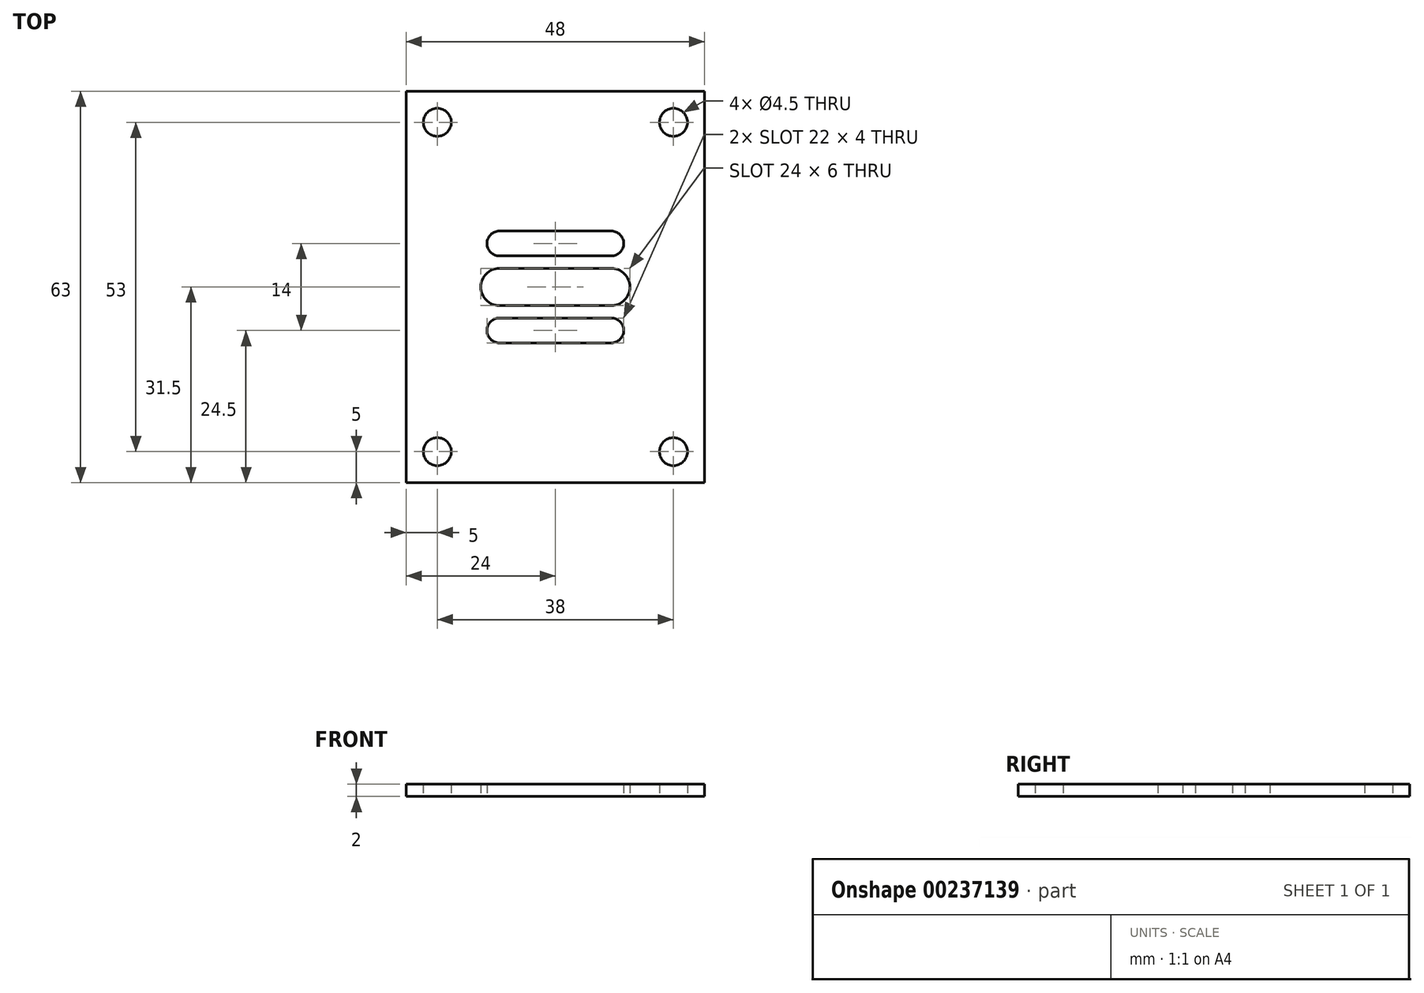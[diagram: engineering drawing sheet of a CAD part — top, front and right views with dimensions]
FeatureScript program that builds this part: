
annotation { "Feature Type Name" : "Feature", "Feature Type Description" : "" }
export const myFeature = defineFeature(function(context is Context, id is Id, definition is map)
    precondition{}
    {
        {
            var Q0;
            Q0=qCreatedBy(makeId("Top.planeOp"),FACE);
            var sketch = newSketch(context, id + "F0", { "sketchPlane" : qUnion([Q0])});
            skLineSegment(sketch, "E0.top", {"start": v(-24, -31.5) * mm, "end": v(24, -31.5) * mm});
            skLineSegment(sketch, "E0.left", {"start": v(-24, 31.5) * mm, "end": v(-24, -31.5) * mm});
            skLineSegment(sketch, "E0.right", {"start": v(24, 31.5) * mm, "end": v(24, -31.5) * mm});
            skPoint(sketch, "E0.middle", {"position": v(0, 0) * mm});
            skLineSegment(sketch, "E1.bottom", {"start": v(-9, 3) * mm, "end": v(9, 3) * mm});
            skLineSegment(sketch, "E1.top", {"start": v(-9, -3) * mm, "end": v(9, -3) * mm});
            skLineSegment(sketch, "E1.left", {"start": v(-12, 0) * mm, "end": v(-12, 0) * mm});
            skLineSegment(sketch, "E1.right", {"start": v(12, 0) * mm, "end": v(12, 0) * mm});
            skArc(sketch, "E2.filletArc", {"start": v(-9, 3) * mm, "mid": v(-11.12, 2.12) * mm, "end": v(-12, 0) * mm});
            skArc(sketch, "E3.filletArc", {"start": v(9, -3) * mm, "mid": v(11.12, -2.12) * mm, "end": v(12, 0) * mm});
            skArc(sketch, "E4.filletArc", {"start": v(12, 0) * mm, "mid": v(11.12, 2.12) * mm, "end": v(9, 3) * mm});
            skArc(sketch, "E5.filletArc", {"start": v(-12, 0) * mm, "mid": v(-11.12, -2.12) * mm, "end": v(-9, -3) * mm});
            skLineSegment(sketch, "E6", {"start": v(-9, 0) * mm, "end": v(-6.45, 0) * mm});
            skLineSegment(sketch, "E7", {"start": v(9, 0) * mm, "end": v(6, 0) * mm});
            skLineSegment(sketch, "E8", {"start": v(4, 0) * mm, "end": v(-4, 0) * mm});
            skLineSegment(sketch, "E9.bottom", {"start": v(-9, -9) * mm, "end": v(9, -9) * mm});
            skLineSegment(sketch, "E9.top", {"start": v(-9, -5) * mm, "end": v(9, -5) * mm});
            skLineSegment(sketch, "E9.left", {"start": v(-11, -7) * mm, "end": v(-11, -7) * mm});
            skLineSegment(sketch, "E9.right", {"start": v(11, -7) * mm, "end": v(11, -7) * mm});
            skPoint(sketch, "E9.middle", {"position": v(0, -7) * mm});
            skArc(sketch, "E10.filletArc", {"start": v(-9, -5) * mm, "mid": v(-10.41, -5.59) * mm, "end": v(-11, -7) * mm});
            skArc(sketch, "E11.filletArc", {"start": v(-11, -7) * mm, "mid": v(-10.41, -8.41) * mm, "end": v(-9, -9) * mm});
            skArc(sketch, "E12.filletArc", {"start": v(9, -9) * mm, "mid": v(10.41, -8.41) * mm, "end": v(11, -7) * mm});
            skArc(sketch, "E13.filletArc", {"start": v(11, -7) * mm, "mid": v(10.41, -5.59) * mm, "end": v(9, -5) * mm});
            skLineSegment(sketch, "E14.bottom", {"start": v(-9, 9) * mm, "end": v(9, 9) * mm});
            skLineSegment(sketch, "E14.top", {"start": v(-9, 5) * mm, "end": v(9, 5) * mm});
            skLineSegment(sketch, "E14.left", {"start": v(-11, 7) * mm, "end": v(-11, 7) * mm});
            skLineSegment(sketch, "E14.right", {"start": v(11, 7) * mm, "end": v(11, 7) * mm});
            skPoint(sketch, "E14.middle", {"position": v(0, 7) * mm});
            skArc(sketch, "E15.filletArc", {"start": v(-9, 9) * mm, "mid": v(-10.41, 8.41) * mm, "end": v(-11, 7) * mm});
            skArc(sketch, "E16.filletArc", {"start": v(11, 7) * mm, "mid": v(10.41, 8.41) * mm, "end": v(9, 9) * mm});
            skArc(sketch, "E17.filletArc", {"start": v(9, 5) * mm, "mid": v(10.41, 5.59) * mm, "end": v(11, 7) * mm});
            skArc(sketch, "E18.filletArc", {"start": v(-11, 7) * mm, "mid": v(-10.41, 5.59) * mm, "end": v(-9, 5) * mm});
            skCircle(sketch, "E19", {"center": v(-19, 26.5) * mm, "radius": 2.25 * mm});
            skCircle(sketch, "E20", {"center": v(19, 26.5) * mm, "radius": 2.25 * mm});
            skCircle(sketch, "E21", {"center": v(19, -26.5) * mm, "radius": 2.25 * mm});
            skCircle(sketch, "E22", {"center": v(-19, -26.5) * mm, "radius": 2.25 * mm});
            skLineSegment(sketch, "E23", {"start": v(-19, 31.73) * mm, "end": v(-19, -31.5) * mm, "construction": true});
            skLineSegment(sketch, "E24", {"start": v(19, 31.58) * mm, "end": v(19, -31.5) * mm, "construction": true});
            skLineSegment(sketch, "E25", {"start": v(-24, 26.5) * mm, "end": v(24, 26.5) * mm, "construction": true});
            skLineSegment(sketch, "E26", {"start": v(-24, -26.5) * mm, "end": v(24, -26.5) * mm, "construction": true});
            skLineSegment(sketch, "E27", {"start": v(-24, 31.5) * mm, "end": v(24, 31.5) * mm});
            skSolve(sketch);
        }
        {
            var Q0;
            Q0 = qSketchRegion(id + "F0", true);
            extrude(context, id + "F1", {"entities" : qUnion([Q0]), "depth" : 2 * mm});
        }
    });
